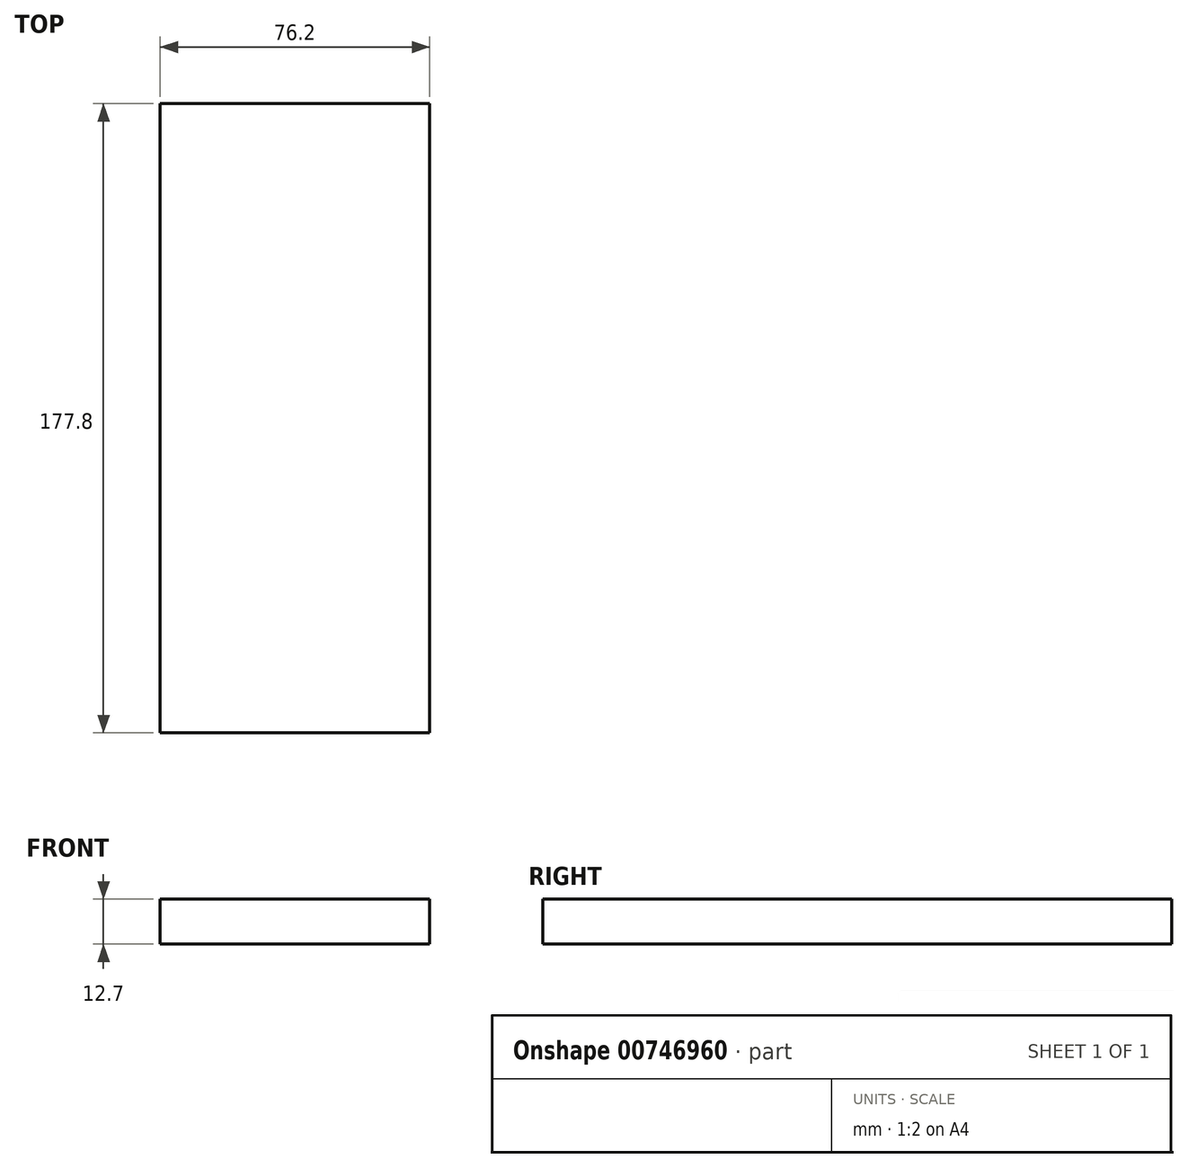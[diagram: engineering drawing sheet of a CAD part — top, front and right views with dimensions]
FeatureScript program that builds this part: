
annotation { "Feature Type Name" : "Feature", "Feature Type Description" : "" }
export const myFeature = defineFeature(function(context is Context, id is Id, definition is map)
    precondition{}
    {
        {
            var Q0;
            Q0=qCreatedBy(makeId("Top.planeOp"),FACE);
            var sketch = newSketch(context, id + "F0", { "sketchPlane" : qUnion([Q0])});
            skLineSegment(sketch, "E0.bottom", {"start": v(-115.13, 151.7) * mm, "end": v(-38.93, 151.7) * mm});
            skLineSegment(sketch, "E0.top", {"start": v(-115.13, -26.1) * mm, "end": v(-38.93, -26.1) * mm});
            skLineSegment(sketch, "E0.left", {"start": v(-115.13, 151.7) * mm, "end": v(-115.13, -26.1) * mm});
            skLineSegment(sketch, "E0.right", {"start": v(-38.93, 151.7) * mm, "end": v(-38.93, -26.1) * mm});
            skSolve(sketch);
        }
        {
            var Q0;
            Q0 = qSketchRegion(id + "F0", true);
            extrude(context, id + "F1", {"entities" : qUnion([Q0]), "depth" : 12.7 * mm, "offsetDistance" : 25.4 * mm});
        }
    });
